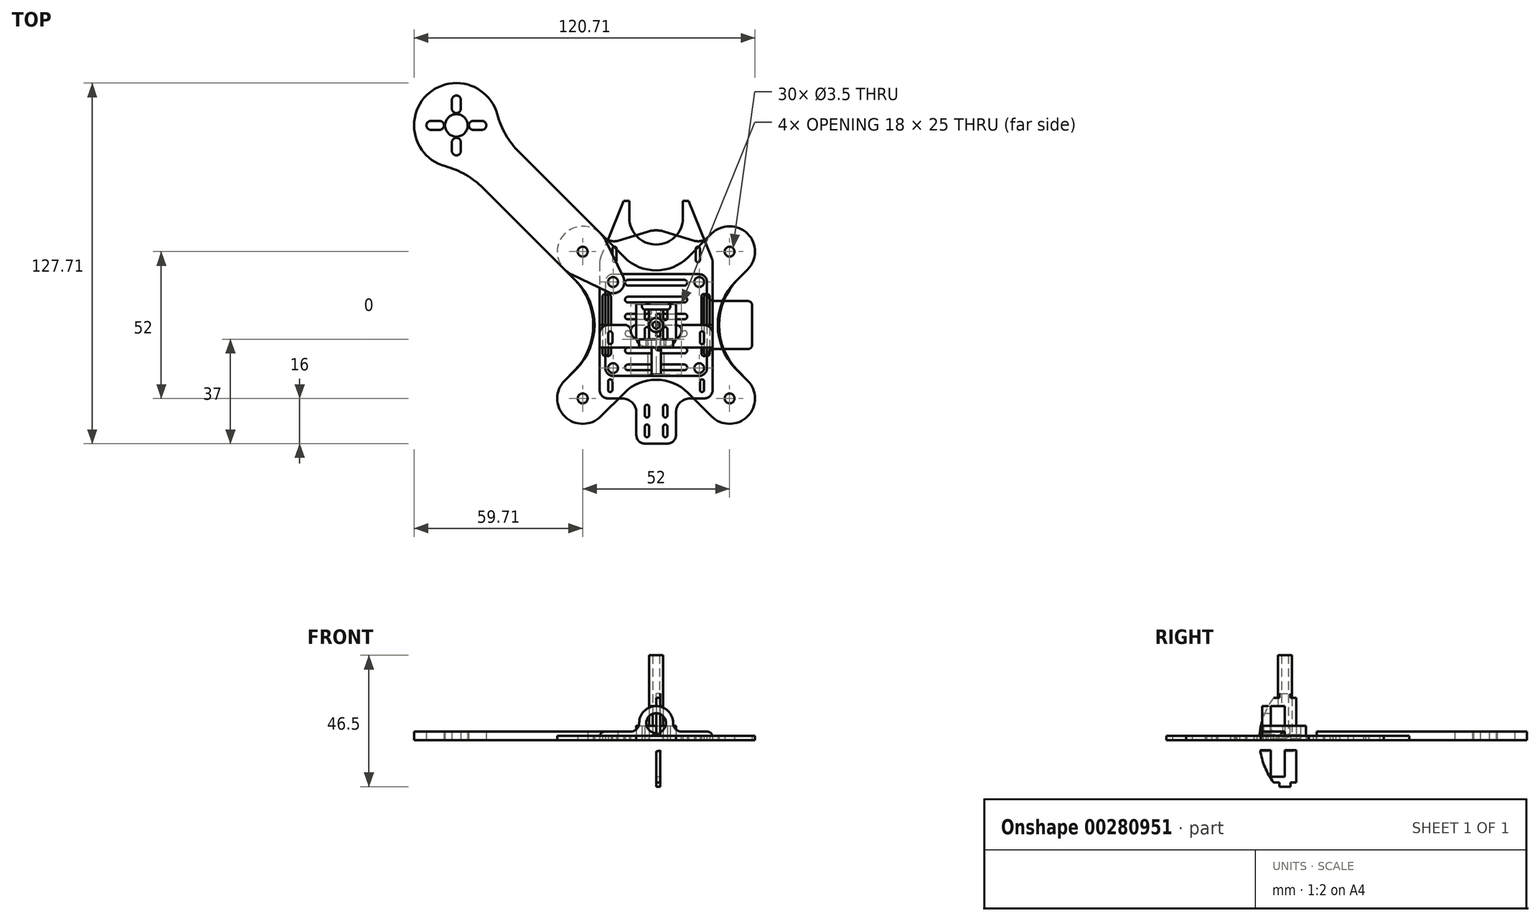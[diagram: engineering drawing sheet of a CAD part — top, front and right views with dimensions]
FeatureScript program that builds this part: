
annotation { "Feature Type Name" : "Feature", "Feature Type Description" : "" }
export const myFeature = defineFeature(function(context is Context, id is Id, definition is map)
    precondition{}
    {
        {
            var Q0;
            Q0=qCreatedBy(makeId("Top.planeOp"),FACE);
            var sketch = newSketch(context, id + "F0", { "sketchPlane" : qUnion([Q0])});
            skCircle(sketch, "E0", {"center": v(0, 0) * mm, "radius": 100 * mm, "construction": true});
            skLineSegment(sketch, "E1", {"start": v(0, 0) * mm, "end": v(70.71, 70.71) * mm, "construction": true});
            skLineSegment(sketch, "E2", {"start": v(0, 0) * mm, "end": v(-70.71, 70.71) * mm, "construction": true});
            skLineSegment(sketch, "E3", {"start": v(0, 0) * mm, "end": v(-70.71, -70.71) * mm, "construction": true});
            skLineSegment(sketch, "E4", {"start": v(0, 0) * mm, "end": v(70.71, -70.71) * mm, "construction": true});
            skArc(sketch, "E5", {"start": v(-56.23, 74.61) * mm, "mid": v(-81.32, 81.32) * mm, "end": v(-74.61, 56.23) * mm});
            skCircle(sketch, "E6", {"center": v(-70.71, 70.71) * mm, "radius": 4 * mm});
            skPoint(sketch, "E7.visualSharp", {"position": v(-68.59, 55.86) * mm});
            skPoint(sketch, "E8.visualSharp", {"position": v(-55.86, 68.59) * mm});
            skLineSegment(sketch, "E9", {"start": v(-70.71, 70.71) * mm, "end": v(-70.71, 85.71) * mm, "construction": true});
            skLineSegment(sketch, "E10", {"start": v(-70.71, 70.71) * mm, "end": v(-85.71, 70.71) * mm, "construction": true});
            skLineSegment(sketch, "E11", {"start": v(-70.71, 70.71) * mm, "end": v(-70.71, 55.71) * mm, "construction": true});
            skLineSegment(sketch, "E12", {"start": v(-70.71, 70.71) * mm, "end": v(-55.71, 70.71) * mm, "construction": true});
            skArc(sketch, "E13", {"start": v(-72.31, 76.71) * mm, "mid": v(-70.71, 75.11) * mm, "end": v(-69.11, 76.71) * mm});
            skArc(sketch, "E14", {"start": v(-69.11, 79.71) * mm, "mid": v(-70.71, 81.31) * mm, "end": v(-72.31, 79.71) * mm});
            skLineSegment(sketch, "E15", {"start": v(-72.31, 79.71) * mm, "end": v(-72.31, 76.71) * mm});
            skLineSegment(sketch, "E16", {"start": v(-69.11, 79.71) * mm, "end": v(-69.11, 76.71) * mm});
            skArc(sketch, "E17.1.0", {"start": v(-76.71, 69.11) * mm, "mid": v(-75.11, 70.71) * mm, "end": v(-76.71, 72.31) * mm});
            skArc(sketch, "E17.1.1", {"start": v(-79.71, 72.31) * mm, "mid": v(-81.31, 70.71) * mm, "end": v(-79.71, 69.11) * mm});
            skLineSegment(sketch, "E17.1.2", {"start": v(-79.71, 72.31) * mm, "end": v(-76.71, 72.31) * mm});
            skLineSegment(sketch, "E17.1.3", {"start": v(-79.71, 69.11) * mm, "end": v(-76.71, 69.11) * mm});
            skArc(sketch, "E17.2.0", {"start": v(-69.11, 64.71) * mm, "mid": v(-70.71, 66.31) * mm, "end": v(-72.31, 64.71) * mm});
            skArc(sketch, "E17.2.1", {"start": v(-72.31, 61.71) * mm, "mid": v(-70.71, 60.11) * mm, "end": v(-69.11, 61.71) * mm});
            skLineSegment(sketch, "E17.2.2", {"start": v(-72.31, 61.71) * mm, "end": v(-72.31, 64.71) * mm});
            skLineSegment(sketch, "E17.2.3", {"start": v(-69.11, 61.71) * mm, "end": v(-69.11, 64.71) * mm});
            skArc(sketch, "E17.3.0", {"start": v(-64.71, 72.31) * mm, "mid": v(-66.31, 70.71) * mm, "end": v(-64.71, 69.11) * mm});
            skArc(sketch, "E17.3.1", {"start": v(-61.71, 69.11) * mm, "mid": v(-60.11, 70.71) * mm, "end": v(-61.71, 72.31) * mm});
            skLineSegment(sketch, "E17.3.2", {"start": v(-61.71, 69.11) * mm, "end": v(-64.71, 69.11) * mm});
            skLineSegment(sketch, "E17.3.3", {"start": v(-61.71, 72.31) * mm, "end": v(-64.71, 72.31) * mm});
            skLineSegment(sketch, "E18", {"start": v(-19.64, 32.36) * mm, "end": v(-48.47, 61.2) * mm});
            skArc(sketch, "E19.filletArc", {"start": v(-61.2, 48.47) * mm, "mid": v(-67.4, 53.23) * mm, "end": v(-74.61, 56.23) * mm});
            skArc(sketch, "E20.filletArc", {"start": v(-56.23, 74.61) * mm, "mid": v(-53.23, 67.4) * mm, "end": v(-48.47, 61.2) * mm});
            skCircle(sketch, "E21", {"center": v(-15.25, 15.25) * mm, "radius": 1.75 * mm});
            skArc(sketch, "E22", {"start": v(-17, 11.65) * mm, "mid": v(-12.42, 12.42) * mm, "end": v(-11.65, 17) * mm});
            skCircle(sketch, "E23", {"center": v(-26, 26) * mm, "radius": 1.75 * mm});
            skLineSegment(sketch, "E24", {"start": v(-17, 11.65) * mm, "end": v(-29.92, 17.9) * mm});
            skLineSegment(sketch, "E25", {"start": v(-11.65, 17) * mm, "end": v(-17.9, 29.92) * mm});
            skArc(sketch, "E26", {"start": v(-32.36, 19.64) * mm, "mid": v(-31.21, 18.66) * mm, "end": v(-29.92, 17.9) * mm});
            skLineSegment(sketch, "E27.trimOffspring", {"start": v(-32.36, 19.64) * mm, "end": v(-61.2, 48.47) * mm});
            skArc(sketch, "E28.trimOffspring", {"start": v(-17.9, 29.92) * mm, "mid": v(-18.66, 31.21) * mm, "end": v(-19.64, 32.36) * mm});
            skSolve(sketch);
        }
        {
            var Q0;
            Q0 = qSketchRegion(id + "F0", true);
            extrude(context, id + "F1", {"entities" : qUnion([Q0]), "depth" : 3 * mm});
        }
        {
            var Q0;
            Q0=qCreatedBy(makeId("Top.planeOp"),FACE);
            var sketch = newSketch(context, id + "F2", { "sketchPlane" : qUnion([Q0])});
            skLineSegment(sketch, "E29", {"start": v(0, 60) * mm, "end": v(0, -60) * mm, "construction": true});
            skLineSegment(sketch, "E30", {"start": v(-60, 0) * mm, "end": v(60, 0) * mm, "construction": true});
            skCircle(sketch, "E31", {"center": v(-70.71, 70.71) * mm, "radius": 64 * mm, "construction": true});
            skCircle(sketch, "E32", {"center": v(0, 0) * mm, "radius": 100 * mm, "construction": true});
            skLineSegment(sketch, "E33", {"start": v(0, 0) * mm, "end": v(-70.71, 70.71) * mm, "construction": true});
            skCircle(sketch, "E34.MirrorC", {"center": v(-70.71, -70.71) * mm, "radius": 64 * mm, "construction": true});
            skCircle(sketch, "E35.MirrorC", {"center": v(70.71, 70.71) * mm, "radius": 64 * mm, "construction": true});
            skCircle(sketch, "E36.MirrorC", {"center": v(70.71, -70.71) * mm, "radius": 64 * mm, "construction": true});
            skCircle(sketch, "E37", {"center": v(-26, 26) * mm, "radius": 1.75 * mm});
            skArc(sketch, "E38", {"start": v(-19.64, 32.36) * mm, "mid": v(-32.36, 32.36) * mm, "end": v(-32.36, 19.64) * mm});
            skLineSegment(sketch, "E39", {"start": v(-32.36, 19.64) * mm, "end": v(-28.28, 15.56) * mm});
            skLineSegment(sketch, "E40", {"start": v(-19.64, 32.36) * mm, "end": v(-18.4, 31.13) * mm});
            skCircle(sketch, "E41", {"center": v(-15.25, 15.25) * mm, "radius": 1.75 * mm});
            skLineSegment(sketch, "E42", {"start": v(-13.4, 29.88) * mm, "end": v(-2.94, 33.1) * mm});
            skPoint(sketch, "E43.visualSharp", {"position": v(-16.27, 29) * mm});
            skArc(sketch, "E43.filletArc", {"start": v(-18.4, 31.13) * mm, "mid": v(-16.07, 29.81) * mm, "end": v(-13.4, 29.88) * mm});
            skLineSegment(sketch, "E44.MirrorCS", {"start": v(19.64, 32.36) * mm, "end": v(18.4, 31.13) * mm});
            skArc(sketch, "E45.MirrorCS", {"start": v(18.4, 31.13) * mm, "mid": v(16.07, 29.81) * mm, "end": v(13.4, 29.88) * mm});
            skPoint(sketch, "E46.MirrorP", {"position": v(16.27, 29) * mm});
            skCircle(sketch, "E47.MirrorC", {"center": v(26, 26) * mm, "radius": 1.75 * mm});
            skLineSegment(sketch, "E48.MirrorCS", {"start": v(32.36, 19.64) * mm, "end": v(28.28, 15.56) * mm});
            skArc(sketch, "E49.MirrorCS", {"start": v(19.64, 32.36) * mm, "mid": v(32.36, 32.36) * mm, "end": v(32.36, 19.64) * mm});
            skLineSegment(sketch, "E50.MirrorCS", {"start": v(13.4, 29.88) * mm, "end": v(2.94, 33.1) * mm});
            skCircle(sketch, "E51.MirrorC", {"center": v(15.25, 15.25) * mm, "radius": 1.75 * mm});
            skLineSegment(sketch, "E52.MirrorCS", {"start": v(60, 0) * mm, "end": v(-60, 0) * mm, "construction": true});
            skLineSegment(sketch, "E53.MirrorCS", {"start": v(19.64, -32.36) * mm, "end": v(11.31, -24.04) * mm});
            skLineSegment(sketch, "E54.MirrorCS", {"start": v(-19.64, -32.36) * mm, "end": v(-11.31, -24.04) * mm});
            skCircle(sketch, "E55.MirrorC", {"center": v(-26, -26) * mm, "radius": 1.75 * mm});
            skLineSegment(sketch, "E56.MirrorCS", {"start": v(-32.36, -19.64) * mm, "end": v(-28.28, -15.56) * mm});
            skArc(sketch, "E57.MirrorCS", {"start": v(19.64, -32.36) * mm, "mid": v(32.36, -32.36) * mm, "end": v(32.36, -19.64) * mm});
            skCircle(sketch, "E58.MirrorC", {"center": v(15.25, -15.25) * mm, "radius": 1.75 * mm});
            skLineSegment(sketch, "E59.MirrorCS", {"start": v(32.36, -19.64) * mm, "end": v(28.28, -15.56) * mm});
            skArc(sketch, "E60.MirrorCS", {"start": v(-19.64, -32.36) * mm, "mid": v(-32.36, -32.36) * mm, "end": v(-32.36, -19.64) * mm});
            skCircle(sketch, "E61.MirrorC", {"center": v(-15.25, -15.25) * mm, "radius": 1.75 * mm});
            skCircle(sketch, "E62.MirrorC", {"center": v(26, -26) * mm, "radius": 1.75 * mm});
            skArc(sketch, "E63", {"start": v(28.28, 15.56) * mm, "mid": v(21.84, 0) * mm, "end": v(28.28, -15.56) * mm});
            skArc(sketch, "E64.MirrorCS", {"start": v(-28.28, 15.56) * mm, "mid": v(-21.84, 0) * mm, "end": v(-28.28, -15.56) * mm});
            skArc(sketch, "E65.trimOffspring", {"start": v(11.31, -24.04) * mm, "mid": v(0, -19.36) * mm, "end": v(-11.31, -24.04) * mm});
            skPoint(sketch, "E66.visualSharp", {"position": v(0, 34) * mm});
            skArc(sketch, "E66.filletArc", {"start": v(2.94, 33.1) * mm, "mid": v(0, 33.54) * mm, "end": v(-2.94, 33.1) * mm});
            skLineSegment(sketch, "E67.bottom", {"start": v(-15.5, 27) * mm, "end": v(-14, 27) * mm, "construction": true});
            skLineSegment(sketch, "E67.top", {"start": v(-15.5, 23) * mm, "end": v(-14, 23) * mm, "construction": true});
            skLineSegment(sketch, "E67.left", {"start": v(-15.5, 27) * mm, "end": v(-15.5, 23) * mm});
            skLineSegment(sketch, "E67.right", {"start": v(-14, 27) * mm, "end": v(-14, 23) * mm});
            skArc(sketch, "E68", {"start": v(-14, 27) * mm, "mid": v(-14.75, 27.75) * mm, "end": v(-15.5, 27) * mm});
            skArc(sketch, "E69", {"start": v(-15.5, 23) * mm, "mid": v(-14.75, 22.25) * mm, "end": v(-14, 23) * mm});
            skLineSegment(sketch, "E70.MirrorCS", {"start": v(15.5, 27) * mm, "end": v(14, 27) * mm, "construction": true});
            skLineSegment(sketch, "E71.MirrorCS", {"start": v(15.5, 23) * mm, "end": v(14, 23) * mm, "construction": true});
            skLineSegment(sketch, "E72.MirrorCS", {"start": v(14, 27) * mm, "end": v(14, 23) * mm});
            skArc(sketch, "E73.MirrorCS", {"start": v(14, 27) * mm, "mid": v(14.75, 27.75) * mm, "end": v(15.5, 27) * mm});
            skLineSegment(sketch, "E74.MirrorCS", {"start": v(15.5, 27) * mm, "end": v(15.5, 23) * mm});
            skArc(sketch, "E75.MirrorCS", {"start": v(15.5, 23) * mm, "mid": v(14.75, 22.25) * mm, "end": v(14, 23) * mm});
            skSolve(sketch);
        }
        {
            var Q0;
            Q0 = qSketchRegion(id + "F2", true);
            extrude(context, id + "F3", {"entities" : qUnion([Q0]), "depth" : 1.5 * mm});
        }
        {
            var Q0;
            Q0=qCreatedBy(makeId("Top.planeOp"),FACE);
            var sketch = newSketch(context, id + "F4", { "sketchPlane" : qUnion([Q0])});
            skLineSegment(sketch, "E76", {"start": v(0, 60) * mm, "end": v(0, -60) * mm, "construction": true});
            skLineSegment(sketch, "E77", {"start": v(-60, 0) * mm, "end": v(60, 0) * mm, "construction": true});
            skCircle(sketch, "E78", {"center": v(-70.71, 70.71) * mm, "radius": 64 * mm, "construction": true});
            skCircle(sketch, "E79", {"center": v(0, 0) * mm, "radius": 100 * mm, "construction": true});
            skLineSegment(sketch, "E80", {"start": v(0, 0) * mm, "end": v(-70.71, 70.71) * mm, "construction": true});
            skCircle(sketch, "E81.MirrorC", {"center": v(-70.71, -70.71) * mm, "radius": 64 * mm, "construction": true});
            skCircle(sketch, "E82.MirrorC", {"center": v(70.71, 70.71) * mm, "radius": 64 * mm, "construction": true});
            skCircle(sketch, "E83.MirrorC", {"center": v(70.71, -70.71) * mm, "radius": 64 * mm, "construction": true});
            skCircle(sketch, "E84", {"center": v(-26, 26) * mm, "radius": 1.75 * mm});
            skArc(sketch, "E85", {"start": v(-19.64, 32.36) * mm, "mid": v(-32.36, 32.36) * mm, "end": v(-32.36, 19.64) * mm});
            skLineSegment(sketch, "E86", {"start": v(-32.36, 19.64) * mm, "end": v(-29, 16.26) * mm});
            skLineSegment(sketch, "E87", {"start": v(-19.64, 32.36) * mm, "end": v(-11.31, 24.04) * mm});
            skCircle(sketch, "E88", {"center": v(-15.25, 15.25) * mm, "radius": 1.75 * mm});
            skLineSegment(sketch, "E89.MirrorCS", {"start": v(19.64, 32.36) * mm, "end": v(11.31, 24.04) * mm});
            skCircle(sketch, "E90.MirrorC", {"center": v(26, 26) * mm, "radius": 1.75 * mm});
            skLineSegment(sketch, "E91.MirrorCS", {"start": v(32.36, 19.64) * mm, "end": v(29, 16.26) * mm});
            skArc(sketch, "E92.MirrorCS", {"start": v(19.64, 32.36) * mm, "mid": v(32.36, 32.36) * mm, "end": v(32.36, 19.64) * mm});
            skCircle(sketch, "E93.MirrorC", {"center": v(15.25, 15.25) * mm, "radius": 1.75 * mm});
            skLineSegment(sketch, "E94.MirrorCS", {"start": v(60, 0) * mm, "end": v(-60, 0) * mm, "construction": true});
            skLineSegment(sketch, "E95.MirrorCS", {"start": v(19.64, -32.36) * mm, "end": v(11.31, -24.04) * mm});
            skLineSegment(sketch, "E96.MirrorCS", {"start": v(-19.64, -32.36) * mm, "end": v(-11.31, -24.04) * mm});
            skCircle(sketch, "E97.MirrorC", {"center": v(-26, -26) * mm, "radius": 1.75 * mm});
            skLineSegment(sketch, "E98.MirrorCS", {"start": v(-32.36, -19.64) * mm, "end": v(-29, -16.26) * mm});
            skArc(sketch, "E99.MirrorCS", {"start": v(19.64, -32.36) * mm, "mid": v(32.36, -32.36) * mm, "end": v(32.36, -19.64) * mm});
            skCircle(sketch, "E100.MirrorC", {"center": v(15.25, -15.25) * mm, "radius": 1.75 * mm});
            skLineSegment(sketch, "E101.MirrorCS", {"start": v(32.36, -19.64) * mm, "end": v(29, -16.26) * mm});
            skArc(sketch, "E102.MirrorCS", {"start": v(-19.64, -32.36) * mm, "mid": v(-32.36, -32.36) * mm, "end": v(-32.36, -19.64) * mm});
            skCircle(sketch, "E103.MirrorC", {"center": v(-15.25, -15.25) * mm, "radius": 1.75 * mm});
            skCircle(sketch, "E104.MirrorC", {"center": v(26, -26) * mm, "radius": 1.75 * mm});
            skArc(sketch, "E105", {"start": v(29, 16.26) * mm, "mid": v(22.25, 0) * mm, "end": v(29, -16.26) * mm});
            skArc(sketch, "E106.MirrorCS", {"start": v(-29, 16.26) * mm, "mid": v(-22.25, 0) * mm, "end": v(-29, -16.26) * mm});
            skArc(sketch, "E107.trimOffspring", {"start": v(11.31, -24.04) * mm, "mid": v(0, -19.36) * mm, "end": v(-11.31, -24.04) * mm});
            skArc(sketch, "E108", {"start": v(-11.31, 24.04) * mm, "mid": v(0, 19.36) * mm, "end": v(11.31, 24.04) * mm});
            skLineSegment(sketch, "E109.bottom", {"start": v(-19, 10) * mm, "end": v(-17, 10) * mm, "construction": true});
            skLineSegment(sketch, "E109.top", {"start": v(-19, -10) * mm, "end": v(-17, -10) * mm, "construction": true});
            skLineSegment(sketch, "E109.left", {"start": v(-19, 10) * mm, "end": v(-19, -10) * mm});
            skLineSegment(sketch, "E109.right", {"start": v(-17, 10) * mm, "end": v(-17, -10) * mm});
            skArc(sketch, "E110", {"start": v(-17, 10) * mm, "mid": v(-18, 11) * mm, "end": v(-19, 10) * mm});
            skArc(sketch, "E111", {"start": v(-19, -10) * mm, "mid": v(-18, -11) * mm, "end": v(-17, -10) * mm});
            skLineSegment(sketch, "E112.MirrorCS", {"start": v(19, 10) * mm, "end": v(17, 10) * mm, "construction": true});
            skLineSegment(sketch, "E113.MirrorCS", {"start": v(19, -10) * mm, "end": v(17, -10) * mm, "construction": true});
            skArc(sketch, "E114.MirrorCS", {"start": v(19, -10) * mm, "mid": v(18, -11) * mm, "end": v(17, -10) * mm});
            skLineSegment(sketch, "E115.MirrorCS", {"start": v(19, 10) * mm, "end": v(19, -10) * mm});
            skArc(sketch, "E116.MirrorCS", {"start": v(17, 10) * mm, "mid": v(18, 11) * mm, "end": v(19, 10) * mm});
            skLineSegment(sketch, "E117.MirrorCS", {"start": v(17, 10) * mm, "end": v(17, -10) * mm});
            skSolve(sketch);
        }
        {
            var Q0;
            Q0 = qSketchRegion(id + "F4", true);
            extrude(context, id + "F5", {"entities" : qUnion([Q0]), "depth" : 1.5 * mm});
        }
        {
            var Q0;
            Q0=qCreatedBy(makeId("Top.planeOp"),FACE);
            var sketch = newSketch(context, id + "F6", { "sketchPlane" : qUnion([Q0])});
            skLineSegment(sketch, "E118.bottom", {"start": v(-15.25, 18) * mm, "end": v(15.25, 18) * mm});
            skLineSegment(sketch, "E118.top", {"start": v(-15.25, -18) * mm, "end": v(15.25, -18) * mm});
            skLineSegment(sketch, "E118.left", {"start": v(-18, 15.25) * mm, "end": v(-18, -15.25) * mm});
            skLineSegment(sketch, "E118.right", {"start": v(18, 15.25) * mm, "end": v(18, -15.25) * mm});
            skCircle(sketch, "E119", {"center": v(-15.25, 15.25) * mm, "radius": 1.75 * mm});
            skCircle(sketch, "E120", {"center": v(15.25, 15.25) * mm, "radius": 1.75 * mm});
            skCircle(sketch, "E121", {"center": v(-15.25, -15.25) * mm, "radius": 1.75 * mm});
            skCircle(sketch, "E122", {"center": v(15.25, -15.25) * mm, "radius": 1.75 * mm});
            skPoint(sketch, "E123.visualSharp", {"position": v(-18, 18) * mm});
            skArc(sketch, "E123.filletArc", {"start": v(-15.25, 18) * mm, "mid": v(-17.2, 17.2) * mm, "end": v(-18, 15.25) * mm});
            skPoint(sketch, "E124.visualSharp", {"position": v(18, 18) * mm});
            skArc(sketch, "E124.filletArc", {"start": v(18, 15.25) * mm, "mid": v(17.2, 17.2) * mm, "end": v(15.25, 18) * mm});
            skPoint(sketch, "E125.visualSharp", {"position": v(18, -18) * mm});
            skArc(sketch, "E125.filletArc", {"start": v(15.25, -18) * mm, "mid": v(17.2, -17.2) * mm, "end": v(18, -15.25) * mm});
            skPoint(sketch, "E126.visualSharp", {"position": v(-18, -18) * mm});
            skArc(sketch, "E126.filletArc", {"start": v(-18, -15.25) * mm, "mid": v(-17.2, -17.2) * mm, "end": v(-15.25, -18) * mm});
            skSolve(sketch);
        }
        {
            var Q0;
            Q0 = qSketchRegion(id + "F6", true);
            extrude(context, id + "F7", {"entities" : qUnion([Q0]), "depth" : 1.5 * mm});
        }
        {
            var Q0;
            Q0=qCreatedBy(makeId("Top.planeOp"),FACE);
            var sketch = newSketch(context, id + "F8", { "sketchPlane" : qUnion([Q0])});
            skLineSegment(sketch, "E127.bottom", {"start": v(-15.25, 18) * mm, "end": v(15.25, 18) * mm});
            skLineSegment(sketch, "E127.top", {"start": v(-15.25, -18) * mm, "end": v(15.25, -18) * mm});
            skLineSegment(sketch, "E127.left", {"start": v(-18, 15.25) * mm, "end": v(-18, -15.25) * mm});
            skLineSegment(sketch, "E127.right", {"start": v(18, 15.25) * mm, "end": v(18, 11.25) * mm});
            skCircle(sketch, "E128", {"center": v(-15.25, 15.25) * mm, "radius": 1.75 * mm});
            skCircle(sketch, "E129", {"center": v(15.25, 15.25) * mm, "radius": 1.75 * mm});
            skCircle(sketch, "E130", {"center": v(-15.25, -15.25) * mm, "radius": 1.75 * mm});
            skCircle(sketch, "E131", {"center": v(15.25, -15.25) * mm, "radius": 1.75 * mm});
            skPoint(sketch, "E132.visualSharp", {"position": v(-18, 18) * mm});
            skArc(sketch, "E132.filletArc", {"start": v(-15.25, 18) * mm, "mid": v(-17.2, 17.2) * mm, "end": v(-18, 15.25) * mm});
            skPoint(sketch, "E133.visualSharp", {"position": v(-18, -18) * mm});
            skArc(sketch, "E133.filletArc", {"start": v(-18, -15.25) * mm, "mid": v(-17.2, -17.2) * mm, "end": v(-15.25, -18) * mm});
            skPoint(sketch, "E134.visualSharp", {"position": v(18, -18) * mm});
            skArc(sketch, "E134.filletArc", {"start": v(15.25, -18) * mm, "mid": v(17.2, -17.2) * mm, "end": v(18, -15.25) * mm});
            skPoint(sketch, "E135.visualSharp", {"position": v(18, 18) * mm});
            skArc(sketch, "E135.filletArc", {"start": v(18, 15.25) * mm, "mid": v(17.2, 17.2) * mm, "end": v(15.25, 18) * mm});
            skLineSegment(sketch, "E136.bottom", {"start": v(20.75, 8.5) * mm, "end": v(32.5, 8.5) * mm});
            skLineSegment(sketch, "E136.top", {"start": v(20.75, -8.5) * mm, "end": v(32.5, -8.5) * mm});
            skLineSegment(sketch, "E136.right", {"start": v(34, 7) * mm, "end": v(34, -7) * mm});
            skLineSegment(sketch, "E137.trimOffspring", {"start": v(18, -11.25) * mm, "end": v(18, -15.25) * mm});
            skPoint(sketch, "E138.visualSharp", {"position": v(34, 8.5) * mm});
            skArc(sketch, "E138.filletArc", {"start": v(34, 7) * mm, "mid": v(33.56, 8.06) * mm, "end": v(32.5, 8.5) * mm});
            skPoint(sketch, "E139.visualSharp", {"position": v(34, -8.5) * mm});
            skArc(sketch, "E139.filletArc", {"start": v(32.5, -8.5) * mm, "mid": v(33.56, -8.06) * mm, "end": v(34, -7) * mm});
            skPoint(sketch, "E140.visualSharp", {"position": v(18, 8.5) * mm});
            skArc(sketch, "E140.filletArc", {"start": v(18, 11.25) * mm, "mid": v(18.8, 9.3) * mm, "end": v(20.75, 8.5) * mm});
            skPoint(sketch, "E141.visualSharp", {"position": v(18, -8.5) * mm});
            skArc(sketch, "E141.filletArc", {"start": v(20.75, -8.5) * mm, "mid": v(18.8, -9.3) * mm, "end": v(18, -11.25) * mm});
            skSolve(sketch);
        }
        {
            var Q0;
            Q0 = qSketchRegion(id + "F8", true);
            extrude(context, id + "F9", {"entities" : qUnion([Q0]), "depth" : 1.5 * mm});
        }
        {
            var Q0;
            Q0=qCreatedBy(makeId("Right.planeOp"),FACE);
            var sketch = newSketch(context, id + "F10", { "sketchPlane" : qUnion([Q0])});
            skLineSegment(sketch, "E142.bottom", {"start": v(-4, 15) * mm, "end": v(-2, 15) * mm});
            skLineSegment(sketch, "E142.top", {"start": v(-4, -15) * mm, "end": v(-2, -15) * mm});
            skLineSegment(sketch, "E142.right", {"start": v(4, 15) * mm, "end": v(4, -15) * mm});
            skLineSegment(sketch, "E143.top", {"start": v(-2, -16.5) * mm, "end": v(2, -16.5) * mm});
            skLineSegment(sketch, "E143.left", {"start": v(-2, -15) * mm, "end": v(-2, -16.5) * mm});
            skLineSegment(sketch, "E143.right", {"start": v(2, -15) * mm, "end": v(2, -16.5) * mm});
            skLineSegment(sketch, "E144.trimOffspring", {"start": v(2, -15) * mm, "end": v(4, -15) * mm});
            skLineSegment(sketch, "E145.MirrorCS", {"start": v(-2, 15) * mm, "end": v(-2, 16.5) * mm});
            skLineSegment(sketch, "E146.MirrorCS", {"start": v(2, 15) * mm, "end": v(2, 16.5) * mm});
            skLineSegment(sketch, "E147.MirrorCS", {"start": v(-2, 16.5) * mm, "end": v(2, 16.5) * mm});
            skLineSegment(sketch, "E148.trimOffspring", {"start": v(2, 15) * mm, "end": v(4, 15) * mm});
            skCircle(sketch, "E149", {"center": v(0, 0) * mm, "radius": 1.6 * mm});
            skArc(sketch, "E150", {"start": v(-4, 15) * mm, "mid": v(-9, 0) * mm, "end": v(-4, -15) * mm});
            skCircle(sketch, "E151", {"center": v(-5, 0) * mm, "radius": 1.6 * mm});
            skSolve(sketch);
        }
        {
            var Q0;
            Q0 = qSketchRegion(id + "F10", true);
            extrude(context, id + "F11", {"entities" : qUnion([Q0]), "depth" : 1.5 * mm});
        }
        {
            var Q0;
            Q0=qCreatedBy(makeId("Top.planeOp"),FACE);
            var sketch = newSketch(context, id + "F12", { "sketchPlane" : qUnion([Q0])});
            skLineSegment(sketch, "E152", {"start": v(0, 60) * mm, "end": v(0, -60) * mm, "construction": true});
            skLineSegment(sketch, "E153", {"start": v(-60, 0) * mm, "end": v(60, 0) * mm, "construction": true});
            skCircle(sketch, "E154", {"center": v(-70.71, 70.71) * mm, "radius": 64 * mm, "construction": true});
            skCircle(sketch, "E155", {"center": v(0, 0) * mm, "radius": 100 * mm, "construction": true});
            skLineSegment(sketch, "E156", {"start": v(0, 0) * mm, "end": v(-70.71, 70.71) * mm, "construction": true});
            skCircle(sketch, "E157.MirrorC", {"center": v(-70.71, -70.71) * mm, "radius": 64 * mm, "construction": true});
            skCircle(sketch, "E158.MirrorC", {"center": v(70.71, 70.71) * mm, "radius": 64 * mm, "construction": true});
            skCircle(sketch, "E159.MirrorC", {"center": v(70.71, -70.71) * mm, "radius": 64 * mm, "construction": true});
            skCircle(sketch, "E160", {"center": v(-15.25, 15.25) * mm, "radius": 1.75 * mm});
            skCircle(sketch, "E161.MirrorC", {"center": v(15.25, 15.25) * mm, "radius": 1.75 * mm});
            skLineSegment(sketch, "E162.MirrorCS", {"start": v(60, 0) * mm, "end": v(-60, 0) * mm, "construction": true});
            skCircle(sketch, "E163.MirrorC", {"center": v(15.25, -15.25) * mm, "radius": 1.75 * mm});
            skCircle(sketch, "E164.MirrorC", {"center": v(-15.25, -15.25) * mm, "radius": 1.75 * mm});
            skLineSegment(sketch, "E165.bottom", {"start": v(-15.5, 27) * mm, "end": v(-14, 27) * mm, "construction": true});
            skLineSegment(sketch, "E165.top", {"start": v(-15.5, 23) * mm, "end": v(-14, 23) * mm, "construction": true});
            skLineSegment(sketch, "E165.left", {"start": v(-15.5, 27) * mm, "end": v(-15.5, 23) * mm});
            skLineSegment(sketch, "E165.right", {"start": v(-14, 27) * mm, "end": v(-14, 23) * mm});
            skArc(sketch, "E166", {"start": v(-14, 27) * mm, "mid": v(-14.75, 27.75) * mm, "end": v(-15.5, 27) * mm});
            skArc(sketch, "E167", {"start": v(-15.5, 23) * mm, "mid": v(-14.75, 22.25) * mm, "end": v(-14, 23) * mm});
            skLineSegment(sketch, "E168.MirrorCS", {"start": v(15.5, 27) * mm, "end": v(14, 27) * mm, "construction": true});
            skLineSegment(sketch, "E169.MirrorCS", {"start": v(15.5, 23) * mm, "end": v(14, 23) * mm, "construction": true});
            skLineSegment(sketch, "E170.MirrorCS", {"start": v(14, 27) * mm, "end": v(14, 23) * mm});
            skArc(sketch, "E171.MirrorCS", {"start": v(14, 27) * mm, "mid": v(14.75, 27.75) * mm, "end": v(15.5, 27) * mm});
            skLineSegment(sketch, "E172.MirrorCS", {"start": v(15.5, 27) * mm, "end": v(15.5, 23) * mm});
            skArc(sketch, "E173.MirrorCS", {"start": v(15.5, 23) * mm, "mid": v(14.75, 22.25) * mm, "end": v(14, 23) * mm});
            skLineSegment(sketch, "E174.left", {"start": v(-20, 22.03) * mm, "end": v(-20, -23) * mm});
            skLineSegment(sketch, "E174.right", {"start": v(20, 22.03) * mm, "end": v(20, -23) * mm});
            skLineSegment(sketch, "E175", {"start": v(-19.64, 23.9) * mm, "end": v(-11.52, 44) * mm});
            skLineSegment(sketch, "E176", {"start": v(-11.52, 44) * mm, "end": v(-9.5, 44) * mm});
            skLineSegment(sketch, "E177", {"start": v(19.64, 23.9) * mm, "end": v(11.52, 44) * mm});
            skLineSegment(sketch, "E178", {"start": v(11.52, 44) * mm, "end": v(9.5, 44) * mm});
            skLineSegment(sketch, "E179", {"start": v(-9.5, 44) * mm, "end": v(-9.5, 38) * mm});
            skLineSegment(sketch, "E180", {"start": v(9.5, 44) * mm, "end": v(9.5, 38) * mm});
            skArc(sketch, "E181", {"start": v(-9.5, 38) * mm, "mid": v(0, 28.5) * mm, "end": v(9.5, 38) * mm});
            skPoint(sketch, "E182.visualSharp", {"position": v(-20, 23) * mm});
            skArc(sketch, "E182.filletArc", {"start": v(-19.64, 23.9) * mm, "mid": v(-19.9, 22.98) * mm, "end": v(-20, 22.03) * mm});
            skPoint(sketch, "E183.visualSharp", {"position": v(20, 23) * mm});
            skArc(sketch, "E183.filletArc", {"start": v(20, 22.03) * mm, "mid": v(19.9, 22.98) * mm, "end": v(19.64, 23.9) * mm});
            skLineSegment(sketch, "E184.bottom", {"start": v(-18, 10) * mm, "end": v(-16, 10) * mm, "construction": true});
            skLineSegment(sketch, "E184.top", {"start": v(-18, -10) * mm, "end": v(-16, -10) * mm, "construction": true});
            skLineSegment(sketch, "E184.left", {"start": v(-18, 10) * mm, "end": v(-18, -10) * mm});
            skLineSegment(sketch, "E184.right", {"start": v(-16, 10) * mm, "end": v(-16, -10) * mm});
            skArc(sketch, "E185", {"start": v(-16, 10) * mm, "mid": v(-17, 11) * mm, "end": v(-18, 10) * mm});
            skArc(sketch, "E186", {"start": v(-18, -10) * mm, "mid": v(-17, -11) * mm, "end": v(-16, -10) * mm});
            skLineSegment(sketch, "E187.bottom", {"start": v(-10, 16) * mm, "end": v(10, 16) * mm});
            skLineSegment(sketch, "E187.top", {"start": v(-10, 14) * mm, "end": v(10, 14) * mm});
            skLineSegment(sketch, "E187.left", {"start": v(-10, 16) * mm, "end": v(-10, 14) * mm, "construction": true});
            skLineSegment(sketch, "E187.right", {"start": v(10, 16) * mm, "end": v(10, 14) * mm, "construction": true});
            skArc(sketch, "E188", {"start": v(-10, 16) * mm, "mid": v(-11, 15) * mm, "end": v(-10, 14) * mm});
            skArc(sketch, "E189", {"start": v(10, 14) * mm, "mid": v(11, 15) * mm, "end": v(10, 16) * mm});
            skLineSegment(sketch, "E190.0.1.0", {"start": v(-10, 10) * mm, "end": v(10, 10) * mm});
            skArc(sketch, "E190.0.1.1", {"start": v(-10, 10) * mm, "mid": v(-11, 9) * mm, "end": v(-10, 8) * mm});
            skLineSegment(sketch, "E190.0.1.2", {"start": v(-10, 8) * mm, "end": v(10, 8) * mm});
            skArc(sketch, "E190.0.1.3", {"start": v(10, 8) * mm, "mid": v(11, 9) * mm, "end": v(10, 10) * mm});
            skLineSegment(sketch, "E190.0.1.4", {"start": v(10, 10) * mm, "end": v(10, 8) * mm, "construction": true});
            skLineSegment(sketch, "E190.0.1.5", {"start": v(-10, 10) * mm, "end": v(-10, 8) * mm, "construction": true});
            skLineSegment(sketch, "E190.0.2.0", {"start": v(-10, 4) * mm, "end": v(10, 4) * mm});
            skArc(sketch, "E190.0.2.1", {"start": v(-10, 4) * mm, "mid": v(-11, 3) * mm, "end": v(-10, 2) * mm});
            skLineSegment(sketch, "E190.0.2.2", {"start": v(-10, 2) * mm, "end": v(10, 2) * mm});
            skArc(sketch, "E190.0.2.3", {"start": v(10, 2) * mm, "mid": v(11, 3) * mm, "end": v(10, 4) * mm});
            skLineSegment(sketch, "E190.0.2.4", {"start": v(10, 4) * mm, "end": v(10, 2) * mm, "construction": true});
            skLineSegment(sketch, "E190.0.2.5", {"start": v(-10, 4) * mm, "end": v(-10, 2) * mm, "construction": true});
            skLineSegment(sketch, "E190.0.3.0", {"start": v(-10, -2) * mm, "end": v(10, -2) * mm});
            skArc(sketch, "E190.0.3.1", {"start": v(-10, -2) * mm, "mid": v(-11, -3) * mm, "end": v(-10, -4) * mm});
            skLineSegment(sketch, "E190.0.3.2", {"start": v(-10, -4) * mm, "end": v(10, -4) * mm});
            skArc(sketch, "E190.0.3.3", {"start": v(10, -4) * mm, "mid": v(11, -3) * mm, "end": v(10, -2) * mm});
            skLineSegment(sketch, "E190.0.3.4", {"start": v(10, -2) * mm, "end": v(10, -4) * mm, "construction": true});
            skLineSegment(sketch, "E190.0.3.5", {"start": v(-10, -2) * mm, "end": v(-10, -4) * mm, "construction": true});
            skLineSegment(sketch, "E190.0.4.0", {"start": v(-10, -8) * mm, "end": v(10, -8) * mm});
            skArc(sketch, "E190.0.4.1", {"start": v(-10, -8) * mm, "mid": v(-11, -9) * mm, "end": v(-10, -10) * mm});
            skLineSegment(sketch, "E190.0.4.2", {"start": v(-10, -10) * mm, "end": v(10, -10) * mm});
            skArc(sketch, "E190.0.4.3", {"start": v(10, -10) * mm, "mid": v(11, -9) * mm, "end": v(10, -8) * mm});
            skLineSegment(sketch, "E190.0.4.4", {"start": v(10, -8) * mm, "end": v(10, -10) * mm, "construction": true});
            skLineSegment(sketch, "E190.0.4.5", {"start": v(-10, -8) * mm, "end": v(-10, -10) * mm, "construction": true});
            skLineSegment(sketch, "E190.0.5.0", {"start": v(-10, -14) * mm, "end": v(10, -14) * mm});
            skArc(sketch, "E190.0.5.1", {"start": v(-10, -14) * mm, "mid": v(-11, -15) * mm, "end": v(-10, -16) * mm});
            skLineSegment(sketch, "E190.0.5.2", {"start": v(-10, -16) * mm, "end": v(10, -16) * mm});
            skArc(sketch, "E190.0.5.3", {"start": v(10, -16) * mm, "mid": v(11, -15) * mm, "end": v(10, -14) * mm});
            skLineSegment(sketch, "E190.0.5.4", {"start": v(10, -14) * mm, "end": v(10, -16) * mm, "construction": true});
            skLineSegment(sketch, "E190.0.5.5", {"start": v(-10, -14) * mm, "end": v(-10, -16) * mm, "construction": true});
            skLineSegment(sketch, "E190.direction1", {"start": v(-10, 14) * mm, "end": v(15, 14) * mm, "construction": true});
            skLineSegment(sketch, "E190.direction2", {"start": v(-10, 14) * mm, "end": v(-10, 8) * mm, "construction": true});
            skLineSegment(sketch, "E191.MirrorCS", {"start": v(18, -10) * mm, "end": v(16, -10) * mm, "construction": true});
            skLineSegment(sketch, "E192.MirrorCS", {"start": v(18, 10) * mm, "end": v(16, 10) * mm, "construction": true});
            skArc(sketch, "E193.MirrorCS", {"start": v(16, 10) * mm, "mid": v(17, 11) * mm, "end": v(18, 10) * mm});
            skLineSegment(sketch, "E194.MirrorCS", {"start": v(16, 10) * mm, "end": v(16, -10) * mm});
            skLineSegment(sketch, "E195.MirrorCS", {"start": v(18, 10) * mm, "end": v(18, -10) * mm});
            skArc(sketch, "E196.MirrorCS", {"start": v(18, -10) * mm, "mid": v(17, -11) * mm, "end": v(16, -10) * mm});
            skLineSegment(sketch, "E197.bottom", {"start": v(4, -36) * mm, "end": v(2.5, -36) * mm, "construction": true});
            skLineSegment(sketch, "E197.top", {"start": v(4, -39) * mm, "end": v(2.5, -39) * mm, "construction": true});
            skLineSegment(sketch, "E197.left", {"start": v(4, -36) * mm, "end": v(4, -39) * mm});
            skLineSegment(sketch, "E197.right", {"start": v(2.5, -36) * mm, "end": v(2.5, -39) * mm});
            skArc(sketch, "E198", {"start": v(4, -36) * mm, "mid": v(3.25, -35.25) * mm, "end": v(2.5, -36) * mm});
            skArc(sketch, "E199", {"start": v(2.5, -39) * mm, "mid": v(3.25, -39.75) * mm, "end": v(4, -39) * mm});
            skLineSegment(sketch, "E200.MirrorCS", {"start": v(-4, -36) * mm, "end": v(-4, -39) * mm});
            skArc(sketch, "E201.MirrorCS", {"start": v(-4, -36) * mm, "mid": v(-3.25, -35.25) * mm, "end": v(-2.5, -36) * mm});
            skLineSegment(sketch, "E202.MirrorCS", {"start": v(-2.5, -36) * mm, "end": v(-2.5, -39) * mm});
            skLineSegment(sketch, "E203.MirrorCS", {"start": v(-4, -36) * mm, "end": v(-2.5, -36) * mm, "construction": true});
            skArc(sketch, "E204.MirrorCS", {"start": v(-2.5, -39) * mm, "mid": v(-3.25, -39.75) * mm, "end": v(-4, -39) * mm});
            skLineSegment(sketch, "E205.MirrorCS", {"start": v(-4, -39) * mm, "end": v(-2.5, -39) * mm, "construction": true});
            skLineSegment(sketch, "E206", {"start": v(17, -26) * mm, "end": v(12, -26) * mm});
            skLineSegment(sketch, "E207", {"start": v(7, -31) * mm, "end": v(7, -39) * mm});
            skLineSegment(sketch, "E208", {"start": v(-17, -26) * mm, "end": v(-12, -26) * mm});
            skLineSegment(sketch, "E209", {"start": v(-7, -31) * mm, "end": v(-7, -39) * mm});
            skLineSegment(sketch, "E210.trimOffspring", {"start": v(-4, -42) * mm, "end": v(4, -42) * mm});
            skPoint(sketch, "E211.visualSharp", {"position": v(-7, -42) * mm});
            skArc(sketch, "E211.filletArc", {"start": v(-7, -39) * mm, "mid": v(-6.12, -41.12) * mm, "end": v(-4, -42) * mm});
            skPoint(sketch, "E212.visualSharp", {"position": v(7, -42) * mm});
            skArc(sketch, "E212.filletArc", {"start": v(4, -42) * mm, "mid": v(6.12, -41.12) * mm, "end": v(7, -39) * mm});
            skPoint(sketch, "E213.visualSharp", {"position": v(-7, -26) * mm});
            skArc(sketch, "E213.filletArc", {"start": v(-7, -31) * mm, "mid": v(-8.46, -27.46) * mm, "end": v(-12, -26) * mm});
            skPoint(sketch, "E214.visualSharp", {"position": v(7, -26) * mm});
            skArc(sketch, "E214.filletArc", {"start": v(12, -26) * mm, "mid": v(8.46, -27.46) * mm, "end": v(7, -31) * mm});
            skPoint(sketch, "E215.visualSharp", {"position": v(-20, -26) * mm});
            skArc(sketch, "E215.filletArc", {"start": v(-20, -23) * mm, "mid": v(-19.12, -25.12) * mm, "end": v(-17, -26) * mm});
            skPoint(sketch, "E216.visualSharp", {"position": v(20, -26) * mm});
            skArc(sketch, "E216.filletArc", {"start": v(17, -26) * mm, "mid": v(19.12, -25.12) * mm, "end": v(20, -23) * mm});
            skLineSegment(sketch, "E217", {"start": v(-7, -34) * mm, "end": v(7, -34) * mm, "construction": true});
            skLineSegment(sketch, "E218.MirrorCS", {"start": v(-4, -32) * mm, "end": v(-2.5, -32) * mm, "construction": true});
            skLineSegment(sketch, "E219.MirrorCS", {"start": v(4, -32) * mm, "end": v(2.5, -32) * mm, "construction": true});
            skLineSegment(sketch, "E220.MirrorCS", {"start": v(4, -29) * mm, "end": v(2.5, -29) * mm, "construction": true});
            skLineSegment(sketch, "E221.MirrorCS", {"start": v(-4, -29) * mm, "end": v(-2.5, -29) * mm, "construction": true});
            skArc(sketch, "E222.MirrorCS", {"start": v(-4, -32) * mm, "mid": v(-3.25, -32.75) * mm, "end": v(-2.5, -32) * mm});
            skArc(sketch, "E223.MirrorCS", {"start": v(2.5, -29) * mm, "mid": v(3.25, -28.25) * mm, "end": v(4, -29) * mm});
            skArc(sketch, "E224.MirrorCS", {"start": v(-2.5, -29) * mm, "mid": v(-3.25, -28.25) * mm, "end": v(-4, -29) * mm});
            skArc(sketch, "E225.MirrorCS", {"start": v(4, -32) * mm, "mid": v(3.25, -32.75) * mm, "end": v(2.5, -32) * mm});
            skLineSegment(sketch, "E226.MirrorCS", {"start": v(-2.5, -32) * mm, "end": v(-2.5, -29) * mm});
            skLineSegment(sketch, "E227.MirrorCS", {"start": v(-4, -32) * mm, "end": v(-4, -29) * mm});
            skLineSegment(sketch, "E228.MirrorCS", {"start": v(2.5, -32) * mm, "end": v(2.5, -29) * mm});
            skLineSegment(sketch, "E229.MirrorCS", {"start": v(4, -32) * mm, "end": v(4, -29) * mm});
            skLineSegment(sketch, "E230.bottom", {"start": v(-17, -20) * mm, "end": v(-15.5, -20) * mm, "construction": true});
            skLineSegment(sketch, "E230.top", {"start": v(-17, -23) * mm, "end": v(-15.5, -23) * mm, "construction": true});
            skLineSegment(sketch, "E230.left", {"start": v(-17, -20) * mm, "end": v(-17, -23) * mm});
            skLineSegment(sketch, "E230.right", {"start": v(-15.5, -20) * mm, "end": v(-15.5, -23) * mm});
            skArc(sketch, "E231", {"start": v(-15.5, -20) * mm, "mid": v(-16.25, -19.25) * mm, "end": v(-17, -20) * mm});
            skArc(sketch, "E232", {"start": v(-17, -23) * mm, "mid": v(-16.25, -23.75) * mm, "end": v(-15.5, -23) * mm});
            skLineSegment(sketch, "E233.MirrorCS", {"start": v(17, -23) * mm, "end": v(15.5, -23) * mm, "construction": true});
            skLineSegment(sketch, "E234.MirrorCS", {"start": v(17, -20) * mm, "end": v(15.5, -20) * mm, "construction": true});
            skLineSegment(sketch, "E235.MirrorCS", {"start": v(15.5, -20) * mm, "end": v(15.5, -23) * mm});
            skArc(sketch, "E236.MirrorCS", {"start": v(17, -23) * mm, "mid": v(16.25, -23.75) * mm, "end": v(15.5, -23) * mm});
            skArc(sketch, "E237.MirrorCS", {"start": v(15.5, -20) * mm, "mid": v(16.25, -19.25) * mm, "end": v(17, -20) * mm});
            skLineSegment(sketch, "E238.MirrorCS", {"start": v(17, -20) * mm, "end": v(17, -23) * mm});
            skSolve(sketch);
        }
        {
            var Q0;
            Q0=makeQuery(id+"F12.imprint","IMPRINT",FACE,{"disambiguationData":[TD([[makeQuery(id+"F12.imprint","IMPRINT",EDGE,{"derivedFrom":sQuery(id+"F12.wireOp",EDGE,"E160")}),-1.0]])]});
            extrude(context, id + "F13", {"entities" : qUnion([Q0]), "depth" : 1.5 * mm});
        }
        {
            var Q0;
            Q0=qCreatedBy(makeId("Top.planeOp"),FACE);
            var sketch = newSketch(context, id + "F14", { "sketchPlane" : qUnion([Q0])});
            skCircle(sketch, "E239", {"center": v(0, 0) * mm, "radius": 2.5 * mm});
            skCircle(sketch, "E240", {"center": v(0, 0) * mm, "radius": 1.25 * mm});
            skSolve(sketch);
        }
        {
            var Q0;
            Q0 = qSketchRegion(id + "F14", true);
            extrude(context, id + "F15", {"entities" : qUnion([Q0]), "depth" : 30 * mm});
        }
        {
            var Q0;
            Q0=qCreatedBy(makeId("Front.planeOp"),FACE);
            var sketch = newSketch(context, id + "F16", { "sketchPlane" : qUnion([Q0])});
            skLineSegment(sketch, "E241.top", {"start": v(-20, 0) * mm, "end": v(20, 0) * mm});
            skLineSegment(sketch, "E241.left", {"start": v(-20, 1) * mm, "end": v(-20, 0) * mm});
            skLineSegment(sketch, "E241.right", {"start": v(20, 1) * mm, "end": v(20, 0) * mm});
            skCircle(sketch, "E242", {"center": v(0, 6) * mm, "radius": 3.5 * mm});
            skLineSegment(sketch, "E243", {"start": v(-18, 3) * mm, "end": v(-9, 3) * mm});
            skLineSegment(sketch, "E244", {"start": v(-6, 6) * mm, "end": v(-6, 6) * mm});
            skLineSegment(sketch, "E245", {"start": v(6, 6) * mm, "end": v(6, 6) * mm});
            skLineSegment(sketch, "E246", {"start": v(9, 3) * mm, "end": v(18, 3) * mm});
            skArc(sketch, "E247", {"start": v(6, 6) * mm, "mid": v(0, 12) * mm, "end": v(-6, 6) * mm});
            skPoint(sketch, "E248.visualSharp", {"position": v(-6, 3) * mm});
            skArc(sketch, "E248.filletArc", {"start": v(-9, 3) * mm, "mid": v(-6.88, 3.88) * mm, "end": v(-6, 6) * mm});
            skPoint(sketch, "E249.visualSharp", {"position": v(6, 3) * mm});
            skArc(sketch, "E249.filletArc", {"start": v(6, 6) * mm, "mid": v(6.88, 3.88) * mm, "end": v(9, 3) * mm});
            skPoint(sketch, "E250.visualSharp", {"position": v(-20, 3) * mm});
            skArc(sketch, "E250.filletArc", {"start": v(-18, 3) * mm, "mid": v(-19.41, 2.41) * mm, "end": v(-20, 1) * mm});
            skPoint(sketch, "E251.visualSharp", {"position": v(20, 3) * mm});
            skArc(sketch, "E251.filletArc", {"start": v(20, 1) * mm, "mid": v(19.41, 2.41) * mm, "end": v(18, 3) * mm});
            skSolve(sketch);
        }
        {
            var Q0;
            Q0=makeQuery(id+"F16.imprint","IMPRINT",FACE,{"disambiguationData":[TD([[makeQuery(id+"F16.imprint","IMPRINT",EDGE,{"derivedFrom":sQuery(id+"F16.wireOp",EDGE,"E241.top")}),1.0]])]});
            extrude(context, id + "F17", {"entities" : qUnion([Q0]), "depth" : 8 * mm});
        }
        {
            var Q0;
            Q0=makeQuery(id+"F17.opExtrude","SWEPT_FACE",FACE,{"disambiguationData":[OSD([sQuery(id+"F16.wireOp",EDGE,"E241.top")])]});
            var sketch = newSketch(context, id + "F18", { "sketchPlane" : qUnion([Q0])});
            skLineSegment(sketch, "E252", {"start": v(-20, 3) * mm, "end": v(-20, 0) * mm});
            skLineSegment(sketch, "E253", {"start": v(-20, 0) * mm, "end": v(-17, 0) * mm});
            skArc(sketch, "E254", {"start": v(-20, 3) * mm, "mid": v(-19.12, 0.88) * mm, "end": v(-17, 0) * mm});
            skLineSegment(sketch, "E255.MirrorCS", {"start": v(20, 0) * mm, "end": v(17, 0) * mm});
            skLineSegment(sketch, "E256.MirrorCS", {"start": v(20, 3) * mm, "end": v(20, 0) * mm});
            skArc(sketch, "E257.MirrorCS", {"start": v(20, 3) * mm, "mid": v(19.12, 0.88) * mm, "end": v(17, 0) * mm});
            skLineSegment(sketch, "E258.bottom", {"start": v(-17, 6) * mm, "end": v(-15.5, 6) * mm, "construction": true});
            skLineSegment(sketch, "E258.top", {"start": v(-17, 3) * mm, "end": v(-15.5, 3) * mm, "construction": true});
            skLineSegment(sketch, "E258.left", {"start": v(-17, 6) * mm, "end": v(-17, 3) * mm});
            skLineSegment(sketch, "E258.right", {"start": v(-15.5, 6) * mm, "end": v(-15.5, 3) * mm});
            skArc(sketch, "E259", {"start": v(-15.5, 6) * mm, "mid": v(-16.25, 6.75) * mm, "end": v(-17, 6) * mm});
            skArc(sketch, "E260", {"start": v(-17, 3) * mm, "mid": v(-16.25, 2.25) * mm, "end": v(-15.5, 3) * mm});
            skLineSegment(sketch, "E261.MirrorCS", {"start": v(17, 3) * mm, "end": v(15.5, 3) * mm, "construction": true});
            skLineSegment(sketch, "E262.MirrorCS", {"start": v(17, 6) * mm, "end": v(15.5, 6) * mm, "construction": true});
            skArc(sketch, "E263.MirrorCS", {"start": v(17, 3) * mm, "mid": v(16.25, 2.25) * mm, "end": v(15.5, 3) * mm});
            skLineSegment(sketch, "E264.MirrorCS", {"start": v(15.5, 6) * mm, "end": v(15.5, 3) * mm});
            skLineSegment(sketch, "E265.MirrorCS", {"start": v(17, 6) * mm, "end": v(17, 3) * mm});
            skArc(sketch, "E266.MirrorCS", {"start": v(15.5, 6) * mm, "mid": v(16.25, 6.75) * mm, "end": v(17, 6) * mm});
            skSolve(sketch);
        }
        {
            var Q0;
            Q0 = qSketchRegion(id + "F18", true);
            extrude(context, id + "F19", {"entities" : qUnion([Q0]), "operationType" : NewBodyOperationType.REMOVE, "oppositeDirection" : true, "depth" : 25 * mm});
        }
        {
            var Q0;
            Q0=qCreatedBy(makeId("Top.planeOp"),FACE);
            cPlane(context, id + "F20", {"entities" : qUnion([Q0]), "cplaneType" : CPlaneType.OFFSET, "offset" : 12 * mm, "width" : 150 * mm, "height" : 150 * mm});
        }
        {
            var Q0;
            Q0=qCreatedBy(id+"F20.planeOp",FACE);
            var sketch = newSketch(context, id + "F21", { "sketchPlane" : qUnion([Q0])});
            skLineSegment(sketch, "E267.bottom", {"start": v(-9, 0) * mm, "end": v(9, 0) * mm});
            skLineSegment(sketch, "E267.top", {"start": v(-9, -5) * mm, "end": v(9, -5) * mm});
            skLineSegment(sketch, "E267.left", {"start": v(-9, 0) * mm, "end": v(-9, -5) * mm});
            skLineSegment(sketch, "E267.right", {"start": v(9, 0) * mm, "end": v(9, -5) * mm});
            skSolve(sketch);
        }
        {
            var Q0;
            Q0=makeQuery(id+"F21.imprint","IMPRINT",FACE,{"disambiguationData":[TD([[makeQuery(id+"F21.imprint","IMPRINT",EDGE,{"derivedFrom":sQuery(id+"F21.wireOp",EDGE,"E267.bottom")}),-1.0]])]});
            extrude(context, id + "F22", {"entities" : qUnion([Q0]), "operationType" : NewBodyOperationType.REMOVE, "oppositeDirection" : true, "depth" : 25 * mm});
        }
        {
            var Q0;
            Q0=makeQuery(id+"F22.boolean.opBoolean","COPY",EDGE,{"derivedFrom":makeQuery(id+"F22.opExtrude","SWEPT_EDGE",EDGE,{"disambiguationData":[OSD([sQuery(id+"F21.wireOp",EDGE,"E267.top"),sQuery(id+"F21.wireOp",EDGE,"E267.left")])]})});
            var Q1;
            Q1=makeQuery(id+"F22.boolean.opBoolean","COPY",EDGE,{"derivedFrom":makeQuery(id+"F22.opExtrude","SWEPT_EDGE",EDGE,{"disambiguationData":[OSD([sQuery(id+"F21.wireOp",EDGE,"E267.top"),sQuery(id+"F21.wireOp",EDGE,"E267.right")])]})});
            fillet(context, id + "F23", {"entities" : qUnion([Q0, Q1]), "radius" : 3 * mm, "tangentPropagation" : true, "allowEdgeOverflow" : false});
        }
        {
            var Q0;
            Q0=makeQuery(id+"F22.boolean.opBoolean","COPY",EDGE,{"derivedFrom":makeQuery(id+"F22.opExtrude","SWEPT_EDGE",EDGE,{"disambiguationData":[OSD([sQuery(id+"F21.wireOp",EDGE,"E267.bottom"),sQuery(id+"F21.wireOp",EDGE,"E267.left")])]})});
            var Q1;
            Q1=makeQuery(id+"F22.boolean.opBoolean","COPY",EDGE,{"derivedFrom":makeQuery(id+"F22.opExtrude","SWEPT_EDGE",EDGE,{"disambiguationData":[OSD([sQuery(id+"F21.wireOp",EDGE,"E267.bottom"),sQuery(id+"F21.wireOp",EDGE,"E267.right")])]})});
            fillet(context, id + "F24", {"entities" : qUnion([Q0, Q1]), "radius" : 2 * mm, "tangentPropagation" : true, "allowEdgeOverflow" : false});
        }
        {
            var Q0;
            Q0=qCreatedBy(makeId("Top.planeOp"),FACE);
            var sketch = newSketch(context, id + "F25", { "sketchPlane" : qUnion([Q0])});
            skLineSegment(sketch, "E268.bottom", {"start": v(-7, 7.5) * mm, "end": v(7, 7.5) * mm});
            skLineSegment(sketch, "E268.top", {"start": v(-4, -7.5) * mm, "end": v(4, -7.5) * mm});
            skLineSegment(sketch, "E268.left", {"start": v(-7, 7.5) * mm, "end": v(-7, -4.5) * mm});
            skLineSegment(sketch, "E268.right", {"start": v(7, 7.5) * mm, "end": v(7, -4.5) * mm});
            skPoint(sketch, "E269.visualSharp", {"position": v(-7, -7.5) * mm});
            skArc(sketch, "E269.filletArc", {"start": v(-7, -4.5) * mm, "mid": v(-6.12, -6.62) * mm, "end": v(-4, -7.5) * mm});
            skPoint(sketch, "E270.visualSharp", {"position": v(7, -7.5) * mm});
            skArc(sketch, "E270.filletArc", {"start": v(4, -7.5) * mm, "mid": v(6.12, -6.62) * mm, "end": v(7, -4.5) * mm});
            skLineSegment(sketch, "E271.bottom", {"start": v(-4, -1.5) * mm, "end": v(-2.5, -1.5) * mm, "construction": true});
            skLineSegment(sketch, "E271.top", {"start": v(-4, -4.5) * mm, "end": v(-2.5, -4.5) * mm, "construction": true});
            skLineSegment(sketch, "E271.left", {"start": v(-4, -1.5) * mm, "end": v(-4, -4.5) * mm});
            skLineSegment(sketch, "E271.right", {"start": v(-2.5, -1.5) * mm, "end": v(-2.5, -4.5) * mm});
            skArc(sketch, "E272", {"start": v(-2.5, -1.5) * mm, "mid": v(-3.25, -0.75) * mm, "end": v(-4, -1.5) * mm});
            skArc(sketch, "E273", {"start": v(-4, -4.5) * mm, "mid": v(-3.25, -5.25) * mm, "end": v(-2.5, -4.5) * mm});
            skLineSegment(sketch, "E274.MirrorCS", {"start": v(4, -4.5) * mm, "end": v(2.5, -4.5) * mm, "construction": true});
            skLineSegment(sketch, "E275.MirrorCS", {"start": v(4, -1.5) * mm, "end": v(2.5, -1.5) * mm, "construction": true});
            skLineSegment(sketch, "E276.MirrorCS", {"start": v(4, -1.5) * mm, "end": v(4, -4.5) * mm});
            skArc(sketch, "E277.MirrorCS", {"start": v(4, -4.5) * mm, "mid": v(3.25, -5.25) * mm, "end": v(2.5, -4.5) * mm});
            skArc(sketch, "E278.MirrorCS", {"start": v(2.5, -1.5) * mm, "mid": v(3.25, -0.75) * mm, "end": v(4, -1.5) * mm});
            skLineSegment(sketch, "E279.MirrorCS", {"start": v(2.5, -1.5) * mm, "end": v(2.5, -4.5) * mm});
            skLineSegment(sketch, "E280.0.1.0", {"start": v(-4, 5.5) * mm, "end": v(-4, 2.5) * mm});
            skArc(sketch, "E280.0.1.1", {"start": v(-4, 2.5) * mm, "mid": v(-3.25, 1.75) * mm, "end": v(-2.5, 2.5) * mm});
            skLineSegment(sketch, "E280.0.1.2", {"start": v(2.5, 5.5) * mm, "end": v(2.5, 2.5) * mm});
            skLineSegment(sketch, "E280.0.1.3", {"start": v(-2.5, 5.5) * mm, "end": v(-2.5, 2.5) * mm});
            skArc(sketch, "E280.0.1.4", {"start": v(-2.5, 5.5) * mm, "mid": v(-3.25, 6.25) * mm, "end": v(-4, 5.5) * mm});
            skLineSegment(sketch, "E280.0.1.5", {"start": v(4, 5.5) * mm, "end": v(4, 2.5) * mm});
            skArc(sketch, "E280.0.1.6", {"start": v(4, 2.5) * mm, "mid": v(3.25, 1.75) * mm, "end": v(2.5, 2.5) * mm});
            skArc(sketch, "E280.0.1.7", {"start": v(2.5, 5.5) * mm, "mid": v(3.25, 6.25) * mm, "end": v(4, 5.5) * mm});
            skLineSegment(sketch, "E280.0.1.8", {"start": v(4, 5.5) * mm, "end": v(2.5, 5.5) * mm, "construction": true});
            skLineSegment(sketch, "E280.0.1.9", {"start": v(-4, 5.5) * mm, "end": v(-2.5, 5.5) * mm, "construction": true});
            skLineSegment(sketch, "E280.0.1.10", {"start": v(4, 2.5) * mm, "end": v(2.5, 2.5) * mm, "construction": true});
            skLineSegment(sketch, "E280.0.1.11", {"start": v(-4, 2.5) * mm, "end": v(-2.5, 2.5) * mm, "construction": true});
            skLineSegment(sketch, "E280.direction1", {"start": v(-4, -4.5) * mm, "end": v(21, -4.5) * mm, "construction": true});
            skLineSegment(sketch, "E280.direction2", {"start": v(-4, -4.5) * mm, "end": v(-4, 2.5) * mm, "construction": true});
            skSolve(sketch);
        }
        {
            var Q0;
            Q0=makeQuery(id+"F25.imprint","IMPRINT",FACE,{"disambiguationData":[TD([[makeQuery(id+"F25.imprint","IMPRINT",EDGE,{"derivedFrom":sQuery(id+"F25.wireOp",EDGE,"E268.bottom")}),-1.0]])]});
            extrude(context, id + "F26", {"entities" : qUnion([Q0]), "depth" : 5 * mm});
        }
        {
            var Q0;
            Q0=makeQuery(id+"F26.opExtrude","SWEPT_FACE",FACE,{"disambiguationData":[OSD([sQuery(id+"F25.wireOp",EDGE,"E268.bottom")])]});
            var sketch = newSketch(context, id + "F27", { "sketchPlane" : qUnion([Q0])});
            skCircle(sketch, "E281", {"center": v(0, -1) * mm, "radius": 3 * mm});
            skSolve(sketch);
        }
        {
            var Q0;
            Q0 = qSketchRegion(id + "F27", true);
            extrude(context, id + "F28", {"entities" : qUnion([Q0]), "operationType" : NewBodyOperationType.REMOVE, "oppositeDirection" : true, "depth" : 25 * mm});
        }
        {
            var Q0;
            Q0=makeQuery(id+"F28.boolean.opBoolean","INTERSECT",EDGE,{"derivedFrom":[makeQuery(id+"F26.opExtrude","SWEPT_FACE",FACE,{"disambiguationData":[OSD([sQuery(id+"F25.wireOp",EDGE,"E268.top")])]}),makeQuery(id+"F28.opExtrude","SWEPT_FACE",FACE,{"disambiguationData":[OSD([sQuery(id+"F27.wireOp",EDGE,"E281")])]})]});
            fillet(context, id + "F29", {"entities" : qUnion([Q0]), "radius" : 1 * mm, "tangentPropagation" : true, "allowEdgeOverflow" : false});
        }
        {
            var Q0;
            Q0=qCreatedBy(makeId("Top.planeOp"),FACE);
            var sketch = newSketch(context, id + "F30", { "sketchPlane" : qUnion([Q0])});
            skLineSegment(sketch, "E282.bottom", {"start": v(-5, 7.5) * mm, "end": v(5, 7.5) * mm});
            skLineSegment(sketch, "E282.top", {"start": v(-5, 5.5) * mm, "end": v(5, 5.5) * mm});
            skLineSegment(sketch, "E282.left", {"start": v(-5, 7.5) * mm, "end": v(-5, 5.5) * mm});
            skLineSegment(sketch, "E282.right", {"start": v(5, 7.5) * mm, "end": v(5, 5.5) * mm});
            skSolve(sketch);
        }
        {
            var Q0;
            Q0 = qSketchRegion(id + "F30", true);
            extrude(context, id + "F31", {"entities" : qUnion([Q0]), "operationType" : NewBodyOperationType.REMOVE, "depth" : 25 * mm});
        }
        {
            var Q0;
            Q0=makeQuery(id+"F31.boolean.opBoolean","COPY",EDGE,{"derivedFrom":makeQuery(id+"F31.opExtrude","SWEPT_EDGE",EDGE,{"disambiguationData":[OSD([sQuery(id+"F30.wireOp",EDGE,"E282.top"),sQuery(id+"F30.wireOp",EDGE,"E282.right")])]})});
            var Q1;
            Q1=makeQuery(id+"F31.boolean.opBoolean","COPY",EDGE,{"derivedFrom":makeQuery(id+"F31.opExtrude","SWEPT_EDGE",EDGE,{"disambiguationData":[OSD([sQuery(id+"F30.wireOp",EDGE,"E282.top"),sQuery(id+"F30.wireOp",EDGE,"E282.left")])]})});
            fillet(context, id + "F32", {"entities" : qUnion([Q0, Q1]), "radius" : 1 * mm, "tangentPropagation" : true, "allowEdgeOverflow" : false});
        }
    });
